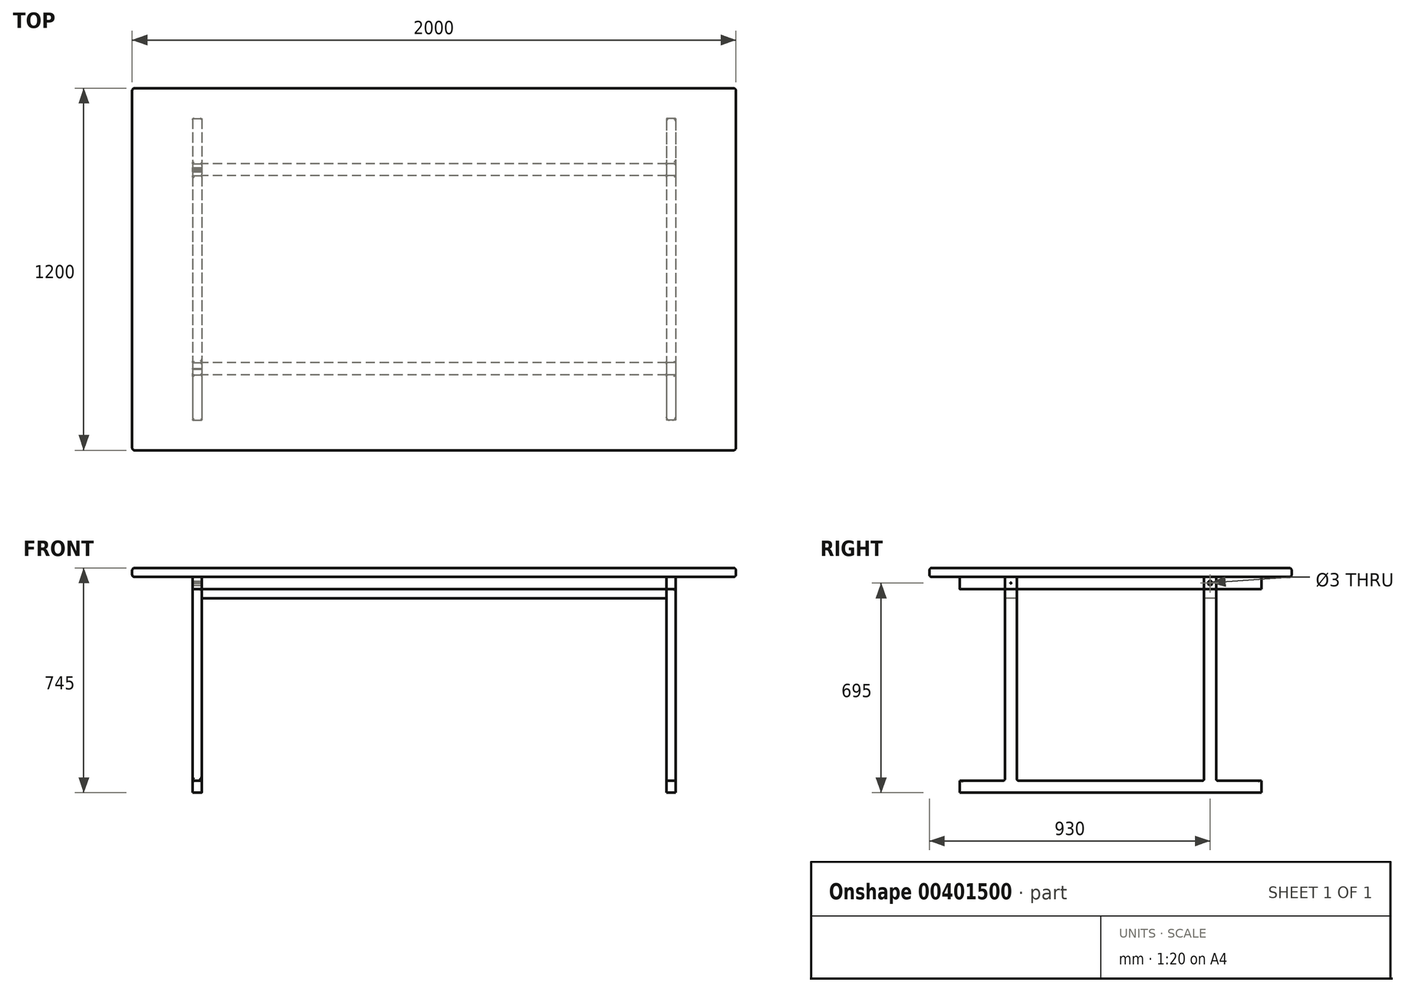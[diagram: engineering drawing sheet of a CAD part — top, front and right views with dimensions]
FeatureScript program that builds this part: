
annotation { "Feature Type Name" : "Feature", "Feature Type Description" : "" }
export const myFeature = defineFeature(function(context is Context, id is Id, definition is map)
    precondition{}
    {
        {
            var Q0;
            Q0=qCreatedBy(makeId("Right.planeOp"),FACE);
            var sketch = newSketch(context, id + "F0", { "sketchPlane" : qUnion([Q0])});
            skLineSegment(sketch, "E0.bottom", {"start": v(600, -15) * mm, "end": v(-600, -15) * mm});
            skLineSegment(sketch, "E0.top", {"start": v(600, 15) * mm, "end": v(-600, 15) * mm});
            skLineSegment(sketch, "E0.left", {"start": v(600, -15) * mm, "end": v(600, 15) * mm});
            skLineSegment(sketch, "E0.right", {"start": v(-600, -15) * mm, "end": v(-600, 15) * mm});
            skPoint(sketch, "E0.middle", {"position": v(0, 0) * mm});
            skSolve(sketch);
        }
        {
            var Q0;
            Q0=makeQuery(id+"F0.imprint","IMPRINT",FACE,{"disambiguationData":[TD([[makeQuery(id+"F0.imprint","IMPRINT",EDGE,{"derivedFrom":sQuery(id+"F0.wireOp",EDGE,"E0.bottom")}),-1.0]])]});
            extrude(context, id + "F1", {"entities" : qUnion([Q0]), "endBound" : BoundingType.SYMMETRIC, "depth" : 2000 * mm});
        }
        {
            var Q0;
            Q0=qCreatedBy(makeId("Right.planeOp"),FACE);
            var sketch = newSketch(context, id + "F2", { "sketchPlane" : qUnion([Q0])});
            skLineSegment(sketch, "E1.bottom", {"start": v(500, -15) * mm, "end": v(-500, -15) * mm});
            skLineSegment(sketch, "E1.top", {"start": v(500, -55) * mm, "end": v(-500, -55) * mm});
            skLineSegment(sketch, "E1.left", {"start": v(500, -15) * mm, "end": v(500, -55) * mm});
            skLineSegment(sketch, "E1.right", {"start": v(-500, -15) * mm, "end": v(-500, -55) * mm});
            skPoint(sketch, "E1.middle", {"position": v(0, -35) * mm});
            skLineSegment(sketch, "E2.bottom", {"start": v(350, -55) * mm, "end": v(310, -55) * mm});
            skLineSegment(sketch, "E2.top", {"start": v(350, -690) * mm, "end": v(310, -690) * mm});
            skLineSegment(sketch, "E2.left", {"start": v(350, -55) * mm, "end": v(350, -690) * mm});
            skLineSegment(sketch, "E2.right", {"start": v(310, -55) * mm, "end": v(310, -690) * mm});
            skLineSegment(sketch, "E3.MirrorCS", {"start": v(-310, -55) * mm, "end": v(-310, -690) * mm});
            skLineSegment(sketch, "E4.MirrorCS", {"start": v(-350, -55) * mm, "end": v(-350, -690) * mm});
            skLineSegment(sketch, "E5.MirrorCS", {"start": v(-350, -690) * mm, "end": v(-310, -690) * mm});
            skLineSegment(sketch, "E6.MirrorCS", {"start": v(-350, -55) * mm, "end": v(-310, -55) * mm});
            skLineSegment(sketch, "E7", {"start": v(292.32, -372.5) * mm, "end": v(-296.04, -372.5) * mm, "construction": true});
            skPoint(sketch, "E7.startSnap0", {"position": v(350, -372.5) * mm});
            skLineSegment(sketch, "E8.MirrorCS", {"start": v(500, -730) * mm, "end": v(-500, -730) * mm});
            skLineSegment(sketch, "E9.MirrorCS", {"start": v(500, -730) * mm, "end": v(500, -690) * mm});
            skLineSegment(sketch, "E10.MirrorCS", {"start": v(500, -690) * mm, "end": v(-500, -690) * mm});
            skLineSegment(sketch, "E11.MirrorCS", {"start": v(-500, -730) * mm, "end": v(-500, -690) * mm});
            skLineSegment(sketch, "E12", {"start": v(350, -85) * mm, "end": v(310, -85) * mm});
            skLineSegment(sketch, "E13", {"start": v(-310, -85) * mm, "end": v(-350, -85) * mm});
            skLineSegment(sketch, "E14.top", {"start": v(350, -15) * mm, "end": v(310, -15) * mm});
            skLineSegment(sketch, "E14.left", {"start": v(350, -55) * mm, "end": v(350, -15) * mm});
            skLineSegment(sketch, "E14.right", {"start": v(310, -55) * mm, "end": v(310, -15) * mm});
            skLineSegment(sketch, "E15.bottom", {"start": v(-310, -55) * mm, "end": v(-350, -55) * mm});
            skLineSegment(sketch, "E15.top", {"start": v(-310, -15) * mm, "end": v(-350, -15) * mm});
            skLineSegment(sketch, "E15.left", {"start": v(-310, -55) * mm, "end": v(-310, -15) * mm});
            skLineSegment(sketch, "E15.right", {"start": v(-350, -55) * mm, "end": v(-350, -15) * mm});
            skCircle(sketch, "E16", {"center": v(330, -35) * mm, "radius": 7 * mm});
            skPoint(sketch, "E16.centerSnap0", {"position": v(330, -55) * mm});
            skPoint(sketch, "E16.centerSnap1", {"position": v(350, -35) * mm});
            skCircle(sketch, "E17", {"center": v(330, -35) * mm, "radius": 1.5 * mm});
            skCircle(sketch, "E18.MirrorC", {"center": v(-330, -35) * mm, "radius": 1.5 * mm});
            skCircle(sketch, "E19.MirrorC", {"center": v(-330, -35) * mm, "radius": 7 * mm});
            skSolve(sketch);
        }
        {
            var Q0;
            Q0=makeQuery(id+"F2.imprint","IMPRINT",FACE,{"disambiguationData":[TD([[makeQuery(id+"F2.imprint","IMPRINT",EDGE,{"derivedFrom":sQuery(id+"F2.wireOp",EDGE,"E8.MirrorCS")}),-1.0]])]});
            var Q1;
            {var subQ3=sQuery(id+"F2.wireOp",EDGE,"E12");Q1=makeQuery(id+"F2.imprint","IMPRINT",FACE,{"disambiguationData":[TD([[makeQuery(id+"F2.imprint","IMPRINT",EDGE,{"derivedFrom":subQ3}),1.0]])]});}
            var Q2;
            {var subQ3=sQuery(id+"F2.wireOp",EDGE,"E13");Q2=makeQuery(id+"F2.imprint","IMPRINT",FACE,{"disambiguationData":[TD([[makeQuery(id+"F2.imprint","IMPRINT",EDGE,{"derivedFrom":subQ3}),1.0]])]});}
            var Q3;
            {var subQ0=sQuery(id+"F2.wireOp",EDGE,"E6.MirrorCS");Q3=makeQuery(id+"F2.imprint","IMPRINT",FACE,{"disambiguationData":[TD([[makeQuery(id+"F2.imprint","IMPRINT",EDGE,{"derivedFrom":subQ0}),-1.0]])]});}
            var Q4;
            {var subQ0=sQuery(id+"F2.wireOp",EDGE,"E2.bottom");Q4=makeQuery(id+"F2.imprint","IMPRINT",FACE,{"disambiguationData":[TD([[makeQuery(id+"F2.imprint","IMPRINT",EDGE,{"derivedFrom":subQ0}),1.0]])]});}
            var Q5;
            Q5=makeQuery(id+"F2.imprint","IMPRINT",FACE,{"disambiguationData":[TD([[makeQuery(id+"F2.imprint","IMPRINT",EDGE,{"derivedFrom":sQuery(id+"F2.wireOp",EDGE,"E1.bottom")}),1.0]])]});
            var Q6;
            {var subQ3=sQuery(id+"F2.wireOp",EDGE,"E12");Q6=makeQuery(id+"F2.imprint","IMPRINT",FACE,{"disambiguationData":[TD([[makeQuery(id+"F2.imprint","IMPRINT",EDGE,{"derivedFrom":subQ3}),-1.0]])]});}
            var Q7;
            Q7=makeQuery(id+"F2.imprint","IMPRINT",FACE,{"disambiguationData":[TD([[makeQuery(id+"F2.imprint","IMPRINT",EDGE,{"derivedFrom":sQuery(id+"F2.wireOp",EDGE,"E2.bottom")}),-1.0]])]});
            var Q8;
            {var subQ3=sQuery(id+"F2.wireOp",EDGE,"E13");Q8=makeQuery(id+"F2.imprint","IMPRINT",FACE,{"disambiguationData":[TD([[makeQuery(id+"F2.imprint","IMPRINT",EDGE,{"derivedFrom":subQ3}),-1.0]])]});}
            var Q9;
            Q9=makeQuery(id+"F2.imprint","IMPRINT",FACE,{"disambiguationData":[TD([[makeQuery(id+"F2.imprint","IMPRINT",EDGE,{"derivedFrom":sQuery(id+"F2.wireOp",EDGE,"E15.bottom")}),-1.0]])]});
            extrude(context, id + "F3", {"entities" : qUnion([Q0, Q1, Q2, Q3, Q4, Q5, Q6, Q7, Q8, Q9]), "depth" : 800 * mm, "hasSecondDirection" : true, "secondDirectionOppositeDirection" : false, "secondDirectionDepth" : 770 * mm});
        }
        {
            var Q0;
            Q0=makeQuery(id+"F2.imprint","IMPRINT",FACE,{"disambiguationData":[TD([[makeQuery(id+"F2.imprint","IMPRINT",EDGE,{"derivedFrom":sQuery(id+"F2.wireOp",EDGE,"E1.bottom")}),1.0]])]});
            var Q1;
            {var subQ0=sQuery(id+"F2.wireOp",EDGE,"E2.bottom");Q1=makeQuery(id+"F2.imprint","IMPRINT",FACE,{"disambiguationData":[TD([[makeQuery(id+"F2.imprint","IMPRINT",EDGE,{"derivedFrom":subQ0}),1.0]])]});}
            var Q2;
            {var subQ3=sQuery(id+"F2.wireOp",EDGE,"E12");Q2=makeQuery(id+"F2.imprint","IMPRINT",FACE,{"disambiguationData":[TD([[makeQuery(id+"F2.imprint","IMPRINT",EDGE,{"derivedFrom":subQ3}),1.0]])]});}
            var Q3;
            Q3=makeQuery(id+"F2.imprint","IMPRINT",FACE,{"disambiguationData":[TD([[makeQuery(id+"F2.imprint","IMPRINT",EDGE,{"derivedFrom":sQuery(id+"F2.wireOp",EDGE,"E8.MirrorCS")}),-1.0]])]});
            var Q4;
            {var subQ3=sQuery(id+"F2.wireOp",EDGE,"E13");Q4=makeQuery(id+"F2.imprint","IMPRINT",FACE,{"disambiguationData":[TD([[makeQuery(id+"F2.imprint","IMPRINT",EDGE,{"derivedFrom":subQ3}),1.0]])]});}
            var Q5;
            {var subQ0=sQuery(id+"F2.wireOp",EDGE,"E6.MirrorCS");Q5=makeQuery(id+"F2.imprint","IMPRINT",FACE,{"disambiguationData":[TD([[makeQuery(id+"F2.imprint","IMPRINT",EDGE,{"derivedFrom":subQ0}),-1.0]])]});}
            var Q6;
            {var subQ3=sQuery(id+"F2.wireOp",EDGE,"E13");Q6=makeQuery(id+"F2.imprint","IMPRINT",FACE,{"disambiguationData":[TD([[makeQuery(id+"F2.imprint","IMPRINT",EDGE,{"derivedFrom":subQ3}),-1.0]])]});}
            var Q7;
            Q7=makeQuery(id+"F2.imprint","IMPRINT",FACE,{"disambiguationData":[TD([[makeQuery(id+"F2.imprint","IMPRINT",EDGE,{"derivedFrom":sQuery(id+"F2.wireOp",EDGE,"E15.bottom")}),-1.0]])]});
            var Q8;
            Q8=makeQuery(id+"F2.imprint","IMPRINT",FACE,{"disambiguationData":[TD([[makeQuery(id+"F2.imprint","IMPRINT",EDGE,{"derivedFrom":sQuery(id+"F2.wireOp",EDGE,"E2.bottom")}),-1.0]])]});
            var Q9;
            {var subQ3=sQuery(id+"F2.wireOp",EDGE,"E12");Q9=makeQuery(id+"F2.imprint","IMPRINT",FACE,{"disambiguationData":[TD([[makeQuery(id+"F2.imprint","IMPRINT",EDGE,{"derivedFrom":subQ3}),-1.0]])]});}
            var Q10;
            Q10=makeQuery(id+"F2.imprint","IMPRINT",FACE,{"disambiguationData":[TD([[makeQuery(id+"F2.imprint","IMPRINT",EDGE,{"derivedFrom":sQuery(id+"F2.wireOp",EDGE,"E16")}),1.0]])]});
            var Q11;
            Q11=makeQuery(id+"F2.imprint","IMPRINT",FACE,{"disambiguationData":[TD([[makeQuery(id+"F2.imprint","IMPRINT",EDGE,{"derivedFrom":sQuery(id+"F2.wireOp",EDGE,"E18.MirrorC")}),1.0]])]});
            extrude(context, id + "F4", {"entities" : qUnion([Q0, Q1, Q2, Q3, Q4, Q5, Q6, Q7, Q8, Q9, Q10, Q11]), "oppositeDirection" : true, "depth" : 800 * mm, "hasSecondDirection" : true, "secondDirectionOppositeDirection" : true, "secondDirectionDepth" : 770 * mm});
        }
        {
            var Q0;
            {var subQ3=sQuery(id+"F2.wireOp",EDGE,"E13");Q0=makeQuery(id+"F2.imprint","IMPRINT",FACE,{"disambiguationData":[TD([[makeQuery(id+"F2.imprint","IMPRINT",EDGE,{"derivedFrom":subQ3}),-1.0]])]});}
            var Q1;
            Q1=makeQuery(id+"F2.imprint","IMPRINT",FACE,{"disambiguationData":[TD([[makeQuery(id+"F2.imprint","IMPRINT",EDGE,{"derivedFrom":sQuery(id+"F2.wireOp",EDGE,"E15.bottom")}),-1.0]])]});
            var Q2;
            {var subQ3=sQuery(id+"F2.wireOp",EDGE,"E12");Q2=makeQuery(id+"F2.imprint","IMPRINT",FACE,{"disambiguationData":[TD([[makeQuery(id+"F2.imprint","IMPRINT",EDGE,{"derivedFrom":subQ3}),-1.0]])]});}
            var Q3;
            Q3=makeQuery(id+"F2.imprint","IMPRINT",FACE,{"disambiguationData":[TD([[makeQuery(id+"F2.imprint","IMPRINT",EDGE,{"derivedFrom":sQuery(id+"F2.wireOp",EDGE,"E2.bottom")}),-1.0]])]});
            extrude(context, id + "F5", {"entities" : qUnion([Q0, Q1, Q2, Q3]), "endBound" : BoundingType.SYMMETRIC, "depth" : 1540 * mm});
        }
        {
            var Q0;
            Q0=makeQuery(id+"F1.opExtrude","SWEPT_FACE",FACE,{"disambiguationData":[OSD([sQuery(id+"F0.wireOp",EDGE,"E0.top")])]});
            var Q1;
            Q1=makeQuery(id+"F1.opExtrude","CAP_EDGE",EDGE,{"disambiguationData":[OSD([sQuery(id+"F0.wireOp",EDGE,"E0.right")])],"isStart":false});
            var Q2;
            Q2=makeQuery(id+"F1.opExtrude","SWEPT_FACE",FACE,{"disambiguationData":[OSD([sQuery(id+"F0.wireOp",EDGE,"E0.bottom")])]});
            var Q3;
            Q3=makeQuery(id+"F1.opExtrude","CAP_EDGE",EDGE,{"disambiguationData":[OSD([sQuery(id+"F0.wireOp",EDGE,"E0.right")])],"isStart":true});
            var Q4;
            Q4=makeQuery(id+"F1.opExtrude","CAP_EDGE",EDGE,{"disambiguationData":[OSD([sQuery(id+"F0.wireOp",EDGE,"E0.left")])],"isStart":false});
            var Q5;
            Q5=makeQuery(id+"F1.opExtrude","CAP_EDGE",EDGE,{"disambiguationData":[OSD([sQuery(id+"F0.wireOp",EDGE,"E0.left")])],"isStart":true});
            fillet(context, id + "F6", {"entities" : qUnion([Q0, Q1, Q2, Q3, Q4, Q5]), "radius" : 8 * mm, "tangentPropagation" : true, "allowEdgeOverflow" : false});
        }
        {
            var Q0;
            {var subQ0=sQuery(id+"F2.wireOp",EDGE,"E1.top");Q0=makeQuery(id+"F3.opExtrude","CAP_EDGE",EDGE,{"disambiguationData":[OSD([subQ0]),TDD([makeQuery(id+"F2.imprint","IMPRINT",EDGE,{"disambiguationData":[TD([[makeQuery(id+"F2.imprint","INTERSECT",VERTEX,{"derivedFrom":[subQ0,sQuery(id+"F2.wireOp",EDGE,"E2.right"),sQuery(id+"F2.wireOp",EDGE,"E2.bottom"),sQuery(id+"F2.wireOp",EDGE,"E14.right")]}),-1.0]])],"derivedFrom":subQ0})])],"isStart":false});}
            var Q1;
            Q1=makeQuery(id+"F3.opExtrude","SWEPT_EDGE",EDGE,{"disambiguationData":[OSD([sQuery(id+"F2.wireOp",EDGE,"E1.top"),sQuery(id+"F2.wireOp",EDGE,"E2.right"),sQuery(id+"F2.wireOp",EDGE,"E2.bottom"),sQuery(id+"F2.wireOp",EDGE,"E14.right")])]});
            var Q2;
            Q2=makeQuery(id+"F3.opExtrude","CAP_EDGE",EDGE,{"disambiguationData":[OSD([sQuery(id+"F2.wireOp",EDGE,"E2.left")])],"isStart":false});
            var Q3;
            Q3=makeQuery(id+"F3.opExtrude","SWEPT_EDGE",EDGE,{"disambiguationData":[OSD([sQuery(id+"F2.wireOp",EDGE,"E1.top"),sQuery(id+"F2.wireOp",EDGE,"E2.left"),sQuery(id+"F2.wireOp",EDGE,"E2.bottom"),sQuery(id+"F2.wireOp",EDGE,"E14.left")])]});
            var Q4;
            Q4=makeQuery(id+"F3.opExtrude","SWEPT_EDGE",EDGE,{"disambiguationData":[OSD([sQuery(id+"F2.wireOp",EDGE,"E1.top"),sQuery(id+"F2.wireOp",EDGE,"E3.MirrorCS"),sQuery(id+"F2.wireOp",EDGE,"E15.bottom"),sQuery(id+"F2.wireOp",EDGE,"E15.left")])]});
            var Q5;
            {var subQ0=sQuery(id+"F2.wireOp",EDGE,"E1.top");Q5=makeQuery(id+"F3.opExtrude","CAP_EDGE",EDGE,{"disambiguationData":[OSD([subQ0]),TDD([makeQuery(id+"F2.imprint","IMPRINT",EDGE,{"disambiguationData":[TD([[makeQuery(id+"F2.imprint","INTERSECT",VERTEX,{"derivedFrom":[subQ0,sQuery(id+"F2.wireOp",EDGE,"E1.right")]}),1.0]])],"derivedFrom":subQ0})])],"isStart":false});}
            var Q6;
            Q6=makeQuery(id+"F3.opExtrude","SWEPT_EDGE",EDGE,{"disambiguationData":[OSD([sQuery(id+"F2.wireOp",EDGE,"E1.top"),sQuery(id+"F2.wireOp",EDGE,"E4.MirrorCS"),sQuery(id+"F2.wireOp",EDGE,"E15.bottom"),sQuery(id+"F2.wireOp",EDGE,"E15.right")])]});
            var Q7;
            Q7=makeQuery(id+"F3.opExtrude","SWEPT_EDGE",EDGE,{"disambiguationData":[OSD([sQuery(id+"F2.wireOp",EDGE,"E4.MirrorCS"),sQuery(id+"F2.wireOp",EDGE,"E10.MirrorCS")])]});
            var Q8;
            Q8=makeQuery(id+"F3.opExtrude","SWEPT_EDGE",EDGE,{"disambiguationData":[OSD([sQuery(id+"F2.wireOp",EDGE,"E3.MirrorCS"),sQuery(id+"F2.wireOp",EDGE,"E10.MirrorCS")])]});
            var Q9;
            Q9=makeQuery(id+"F3.opExtrude","SWEPT_EDGE",EDGE,{"disambiguationData":[OSD([sQuery(id+"F2.wireOp",EDGE,"E2.left"),sQuery(id+"F2.wireOp",EDGE,"E10.MirrorCS")])]});
            var Q10;
            Q10=makeQuery(id+"F3.opExtrude","SWEPT_EDGE",EDGE,{"disambiguationData":[OSD([sQuery(id+"F2.wireOp",EDGE,"E2.right"),sQuery(id+"F2.wireOp",EDGE,"E10.MirrorCS")])]});
            var Q11;
            {var subQ0=sQuery(id+"F2.wireOp",EDGE,"E1.top");Q11=makeQuery(id+"F4.opExtrude","CAP_EDGE",EDGE,{"disambiguationData":[OSD([subQ0]),TDD([makeQuery(id+"F2.imprint","IMPRINT",EDGE,{"disambiguationData":[TD([[makeQuery(id+"F2.imprint","INTERSECT",VERTEX,{"derivedFrom":[subQ0,sQuery(id+"F2.wireOp",EDGE,"E1.right")]}),1.0]])],"derivedFrom":subQ0})])],"isStart":false});}
            var Q12;
            Q12=makeQuery(id+"F4.opExtrude","SWEPT_EDGE",EDGE,{"disambiguationData":[OSD([sQuery(id+"F2.wireOp",EDGE,"E1.top"),sQuery(id+"F2.wireOp",EDGE,"E4.MirrorCS"),sQuery(id+"F2.wireOp",EDGE,"E15.bottom"),sQuery(id+"F2.wireOp",EDGE,"E15.right")])]});
            var Q13;
            {var subQ0=sQuery(id+"F2.wireOp",EDGE,"E1.top");Q13=makeQuery(id+"F4.opExtrude","CAP_EDGE",EDGE,{"disambiguationData":[OSD([subQ0]),TDD([makeQuery(id+"F2.imprint","IMPRINT",EDGE,{"disambiguationData":[TD([[makeQuery(id+"F2.imprint","INTERSECT",VERTEX,{"derivedFrom":[subQ0,sQuery(id+"F2.wireOp",EDGE,"E2.right"),sQuery(id+"F2.wireOp",EDGE,"E2.bottom"),sQuery(id+"F2.wireOp",EDGE,"E14.right")]}),-1.0]])],"derivedFrom":subQ0})])],"isStart":false});}
            var Q14;
            Q14=makeQuery(id+"F4.opExtrude","SWEPT_EDGE",EDGE,{"disambiguationData":[OSD([sQuery(id+"F2.wireOp",EDGE,"E1.top"),sQuery(id+"F2.wireOp",EDGE,"E3.MirrorCS"),sQuery(id+"F2.wireOp",EDGE,"E15.bottom"),sQuery(id+"F2.wireOp",EDGE,"E15.left")])]});
            var Q15;
            Q15=makeQuery(id+"F4.opExtrude","SWEPT_EDGE",EDGE,{"disambiguationData":[OSD([sQuery(id+"F2.wireOp",EDGE,"E1.top"),sQuery(id+"F2.wireOp",EDGE,"E2.right"),sQuery(id+"F2.wireOp",EDGE,"E2.bottom"),sQuery(id+"F2.wireOp",EDGE,"E14.right")])]});
            var Q16;
            {var subQ0=sQuery(id+"F2.wireOp",EDGE,"E1.top");Q16=makeQuery(id+"F4.opExtrude","CAP_EDGE",EDGE,{"disambiguationData":[OSD([subQ0]),TDD([makeQuery(id+"F2.imprint","IMPRINT",EDGE,{"disambiguationData":[TD([[makeQuery(id+"F2.imprint","INTERSECT",VERTEX,{"derivedFrom":[subQ0,sQuery(id+"F2.wireOp",EDGE,"E1.left")]}),-1.0]])],"derivedFrom":subQ0})])],"isStart":false});}
            var Q17;
            Q17=makeQuery(id+"F4.opExtrude","SWEPT_EDGE",EDGE,{"disambiguationData":[OSD([sQuery(id+"F2.wireOp",EDGE,"E1.top"),sQuery(id+"F2.wireOp",EDGE,"E2.left"),sQuery(id+"F2.wireOp",EDGE,"E2.bottom"),sQuery(id+"F2.wireOp",EDGE,"E14.left")])]});
            var Q18;
            {var subQ0=sQuery(id+"F2.wireOp",EDGE,"E10.MirrorCS");Q18=makeQuery(id+"F4.opExtrude","CAP_EDGE",EDGE,{"disambiguationData":[OSD([subQ0]),TDD([makeQuery(id+"F2.imprint","IMPRINT",EDGE,{"disambiguationData":[TD([[makeQuery(id+"F2.imprint","INTERSECT",VERTEX,{"derivedFrom":[sQuery(id+"F2.wireOp",EDGE,"E4.MirrorCS"),subQ0]}),-1.0]])],"derivedFrom":subQ0})])],"isStart":false});}
            var Q19;
            Q19=makeQuery(id+"F4.opExtrude","SWEPT_EDGE",EDGE,{"disambiguationData":[OSD([sQuery(id+"F2.wireOp",EDGE,"E4.MirrorCS"),sQuery(id+"F2.wireOp",EDGE,"E10.MirrorCS")])]});
            var Q20;
            Q20=makeQuery(id+"F4.opExtrude","SWEPT_EDGE",EDGE,{"disambiguationData":[OSD([sQuery(id+"F2.wireOp",EDGE,"E3.MirrorCS"),sQuery(id+"F2.wireOp",EDGE,"E10.MirrorCS")])]});
            var Q21;
            Q21=makeQuery(id+"F4.opExtrude","SWEPT_EDGE",EDGE,{"disambiguationData":[OSD([sQuery(id+"F2.wireOp",EDGE,"E2.right"),sQuery(id+"F2.wireOp",EDGE,"E10.MirrorCS")])]});
            var Q22;
            Q22=makeQuery(id+"F4.opExtrude","SWEPT_EDGE",EDGE,{"disambiguationData":[OSD([sQuery(id+"F2.wireOp",EDGE,"E2.left"),sQuery(id+"F2.wireOp",EDGE,"E10.MirrorCS")])]});
            var Q23;
            Q23=makeQuery(id+"F4.opExtrude","CAP_EDGE",EDGE,{"disambiguationData":[OSD([sQuery(id+"F2.wireOp",EDGE,"E9.MirrorCS")])],"isStart":false});
            var Q24;
            Q24=makeQuery(id+"F4.opExtrude","SWEPT_EDGE",EDGE,{"disambiguationData":[OSD([sQuery(id+"F2.wireOp",EDGE,"E9.MirrorCS"),sQuery(id+"F2.wireOp",EDGE,"E10.MirrorCS")])]});
            var Q25;
            Q25=makeQuery(id+"F4.opExtrude","SWEPT_EDGE",EDGE,{"disambiguationData":[OSD([sQuery(id+"F2.wireOp",EDGE,"E10.MirrorCS"),sQuery(id+"F2.wireOp",EDGE,"E11.MirrorCS")])]});
            var Q26;
            Q26=makeQuery(id+"F4.opExtrude","CAP_EDGE",EDGE,{"disambiguationData":[OSD([sQuery(id+"F2.wireOp",EDGE,"E11.MirrorCS")])],"isStart":true});
            var Q27;
            {var subQ0=sQuery(id+"F2.wireOp",EDGE,"E10.MirrorCS");Q27=makeQuery(id+"F4.opExtrude","CAP_EDGE",EDGE,{"disambiguationData":[OSD([subQ0]),TDD([makeQuery(id+"F2.imprint","IMPRINT",EDGE,{"disambiguationData":[TD([[makeQuery(id+"F2.imprint","INTERSECT",VERTEX,{"derivedFrom":[sQuery(id+"F2.wireOp",EDGE,"E4.MirrorCS"),subQ0]}),-1.0]])],"derivedFrom":subQ0})])],"isStart":true});}
            var Q28;
            Q28=makeQuery(id+"F4.opExtrude","CAP_EDGE",EDGE,{"disambiguationData":[OSD([sQuery(id+"F2.wireOp",EDGE,"E3.MirrorCS")])],"isStart":true});
            var Q29;
            {var subQ0=sQuery(id+"F2.wireOp",EDGE,"E10.MirrorCS");Q29=makeQuery(id+"F4.opExtrude","CAP_EDGE",EDGE,{"disambiguationData":[OSD([subQ0]),TDD([makeQuery(id+"F2.imprint","IMPRINT",EDGE,{"disambiguationData":[TD([[makeQuery(id+"F2.imprint","INTERSECT",VERTEX,{"derivedFrom":[sQuery(id+"F2.wireOp",EDGE,"E2.left"),subQ0]}),1.0]])],"derivedFrom":subQ0})])],"isStart":true});}
            var Q30;
            Q30=makeQuery(id+"F4.opExtrude","CAP_EDGE",EDGE,{"disambiguationData":[OSD([sQuery(id+"F2.wireOp",EDGE,"E9.MirrorCS")])],"isStart":true});
            fillet(context, id + "F7", {"entities" : qUnion([Q0, Q1, Q2, Q3, Q4, Q5, Q6, Q7, Q8, Q9, Q10, Q11, Q12, Q13, Q14, Q15, Q16, Q17, Q18, Q19, Q20, Q21, Q22, Q23, Q24, Q25, Q26, Q27, Q28, Q29, Q30]), "radius" : 5 * mm, "tangentPropagation" : true, "allowEdgeOverflow" : false});
        }
        {
            var Q0;
            Q0=makeQuery(id+"F5.opExtrude","SWEPT_EDGE",EDGE,{"disambiguationData":[OSD([sQuery(id+"F2.wireOp",EDGE,"E2.left"),sQuery(id+"F2.wireOp",EDGE,"E12")])]});
            var Q1;
            Q1=makeQuery(id+"F5.opExtrude","SWEPT_EDGE",EDGE,{"disambiguationData":[OSD([sQuery(id+"F2.wireOp",EDGE,"E2.right"),sQuery(id+"F2.wireOp",EDGE,"E12")])]});
            var Q2;
            Q2=makeQuery(id+"F5.opExtrude","SWEPT_EDGE",EDGE,{"disambiguationData":[OSD([sQuery(id+"F2.wireOp",EDGE,"E4.MirrorCS"),sQuery(id+"F2.wireOp",EDGE,"E13")])]});
            var Q3;
            Q3=makeQuery(id+"F5.opExtrude","SWEPT_EDGE",EDGE,{"disambiguationData":[OSD([sQuery(id+"F2.wireOp",EDGE,"E3.MirrorCS"),sQuery(id+"F2.wireOp",EDGE,"E13")])]});
            var Q4;
            {var subQ0=sQuery(id+"F2.wireOp",EDGE,"E10.MirrorCS");Q4=makeQuery(id+"F3.opExtrude","CAP_EDGE",EDGE,{"disambiguationData":[OSD([subQ0]),TDD([makeQuery(id+"F2.imprint","IMPRINT",EDGE,{"disambiguationData":[TD([[makeQuery(id+"F2.imprint","INTERSECT",VERTEX,{"derivedFrom":[sQuery(id+"F2.wireOp",EDGE,"E2.left"),subQ0]}),1.0]])],"derivedFrom":subQ0})])],"isStart":true});}
            var Q5;
            {var subQ0=sQuery(id+"F2.wireOp",EDGE,"E10.MirrorCS");Q5=makeQuery(id+"F3.opExtrude","CAP_EDGE",EDGE,{"disambiguationData":[OSD([subQ0]),TDD([makeQuery(id+"F2.imprint","IMPRINT",EDGE,{"disambiguationData":[TD([[makeQuery(id+"F2.imprint","INTERSECT",VERTEX,{"derivedFrom":[sQuery(id+"F2.wireOp",EDGE,"E2.right"),subQ0]}),-1.0]])],"derivedFrom":subQ0})])],"isStart":true});}
            var Q6;
            {var subQ0=sQuery(id+"F2.wireOp",EDGE,"E10.MirrorCS");Q6=makeQuery(id+"F3.opExtrude","CAP_EDGE",EDGE,{"disambiguationData":[OSD([subQ0]),TDD([makeQuery(id+"F2.imprint","IMPRINT",EDGE,{"disambiguationData":[TD([[makeQuery(id+"F2.imprint","INTERSECT",VERTEX,{"derivedFrom":[sQuery(id+"F2.wireOp",EDGE,"E4.MirrorCS"),subQ0]}),-1.0]])],"derivedFrom":subQ0})])],"isStart":true});}
            fillet(context, id + "F8", {"entities" : qUnion([Q0, Q1, Q2, Q3, Q4, Q5, Q6]), "radius" : 5 * mm, "tangentPropagation" : true, "allowEdgeOverflow" : false});
        }
        {
            var Q0;
            Q0=makeQuery(id+"F3.opExtrude","CAP_EDGE",EDGE,{"disambiguationData":[OSD([sQuery(id+"F2.wireOp",EDGE,"E9.MirrorCS")])],"isStart":false});
            var Q1;
            Q1=makeQuery(id+"F3.opExtrude","CAP_EDGE",EDGE,{"disambiguationData":[OSD([sQuery(id+"F2.wireOp",EDGE,"E9.MirrorCS")])],"isStart":true});
            var Q2;
            Q2=makeQuery(id+"F3.opExtrude","CAP_EDGE",EDGE,{"disambiguationData":[OSD([sQuery(id+"F2.wireOp",EDGE,"E11.MirrorCS")])],"isStart":true});
            var Q3;
            Q3=makeQuery(id+"F3.opExtrude","CAP_EDGE",EDGE,{"disambiguationData":[OSD([sQuery(id+"F2.wireOp",EDGE,"E11.MirrorCS")])],"isStart":false});
            fillet(context, id + "F9", {"entities" : qUnion([Q0, Q1, Q2, Q3]), "radius" : 10 * mm, "allowEdgeOverflow" : false});
        }
    });
